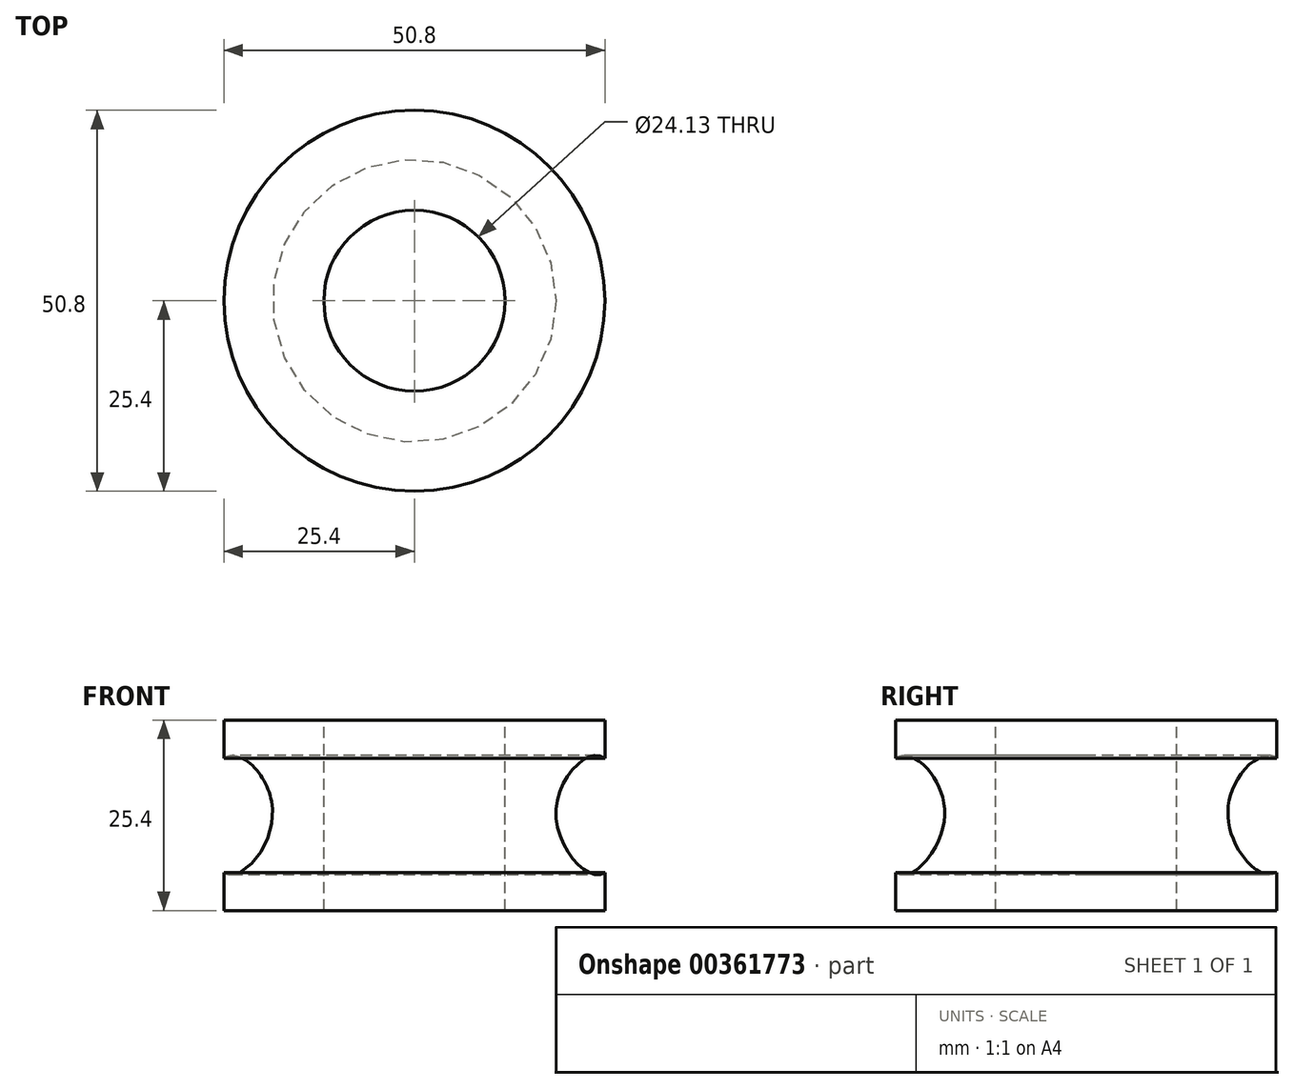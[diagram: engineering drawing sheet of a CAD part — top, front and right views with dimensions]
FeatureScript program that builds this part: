
annotation { "Feature Type Name" : "Feature", "Feature Type Description" : "" }
export const myFeature = defineFeature(function(context is Context, id is Id, definition is map)
    precondition{}
    {
        {
            var Q0;
            Q0=qCreatedBy(makeId("Front.planeOp"),FACE);
            var sketch = newSketch(context, id + "F0", { "sketchPlane" : qUnion([Q0])});
            skLineSegment(sketch, "E0", {"start": v(0, 25.4) * mm, "end": v(0, 0) * mm});
            skLineSegment(sketch, "E1", {"start": v(0, 0) * mm, "end": v(25.4, 0) * mm});
            skLineSegment(sketch, "E2", {"start": v(25.4, 0) * mm, "end": v(25.4, 5.08) * mm});
            skLineSegment(sketch, "E3", {"start": v(0, 25.4) * mm, "end": v(25.4, 25.4) * mm});
            skLineSegment(sketch, "E4", {"start": v(25.4, 25.4) * mm, "end": v(25.4, 20.32) * mm});
            skFitSpline(sketch, "E5", {"points": [v(25.4, 20.32) * mm, v(18.87, 13.15) * mm, v(25.4, 5.08) * mm, v(25.4, 20.32) * mm]});
            skSolve(sketch);
        }
        {
            var Q0;
            Q0=makeQuery(id+"F0.imprint","IMPRINT",FACE,{"disambiguationData":[TD([[makeQuery(id+"F0.imprint","IMPRINT",EDGE,{"derivedFrom":sQuery(id+"F0.wireOp",EDGE,"E0")}),1.0]])]});
            var Q1;
            Q1=sQuery(id+"F0.wireOp",EDGE,"E0");
            revolve(context, id + "F1", {"entities" : qUnion([Q0]), "axis" : qUnion([Q1]), "revolveType" : RevolveType.FULL});
        }
        {
            var Q0;
            Q0=makeQuery(id+"F1.opRevolve","SWEPT_FACE",FACE,{"disambiguationData":[OSD([sQuery(id+"F0.wireOp",EDGE,"E3")])]});
            var sketch = newSketch(context, id + "F2", { "sketchPlane" : qUnion([Q0])});
            skCircle(sketch, "E6", {"center": v(0, 0) * mm, "radius": 12.06 * mm});
            skSolve(sketch);
        }
        {
            var Q0;
            Q0=makeQuery(id+"F2.imprint","IMPRINT",FACE,{"disambiguationData":[TD([[makeQuery(id+"F2.imprint","IMPRINT",EDGE,{"derivedFrom":sQuery(id+"F2.wireOp",EDGE,"E6")}),1.0]])]});
            extrude(context, id + "F3", {"entities" : qUnion([Q0]), "operationType" : NewBodyOperationType.REMOVE, "oppositeDirection" : true, "depth" : 61.72 * mm});
        }
    });
